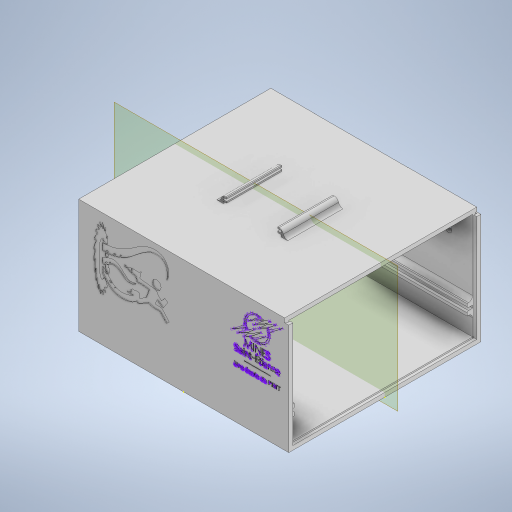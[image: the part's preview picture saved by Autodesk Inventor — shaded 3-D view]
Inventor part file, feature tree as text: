
AUTODESK INVENTOR PART (.ipt)
format: ipt  version: 2023 (Build 270158000, 158)  size: 8,297,472 bytes
history: native  units: mm
features: sketch x25, extrude x21, other x5, fillet x3, projected_geometry x3, sweep x1
ambient origin geometry x8: Origin, YZ Plane, XZ Plane, XY Plane, X Axis, Y Axis, Z Axis, Center Point
bodies: Solide1 (feature_tree)
feature tree (58):
  sketch  "Esquisse1"
  extrude  "Extrusion1"  Depth=133.2mm
  extrude  "Extrusion2"  Depth=146.2mm
  extrude  "Extrusion3"  Depth=3.0mm
  sketch  "Esquisse3"
  extrude  "Extrusion4"  Depth=3.0mm TaperAngle=0.0deg
  extrude  "Extrusion5"  Depth=80.0mm TaperAngle=0.0deg
  extrude  "Extrusion6"  Depth=3.0mm TaperAngle=0.0deg
  extrude  "Extrusion7"  Depth=3.0mm
  extrude  "Extrusion8"  Depth=3.0mm
  fillet  "Congé1"  Radius=3.0mm
  fillet  "Congé2"  Radius=3.0mm
  sketch  "Esquisse9"
  other  "Plan de construction1"
  sketch  "Esquisse11"
  other  "Plan de construction2"
  sweep  "Balayage2"
  sketch  "Esquisse14"
  extrude  "Extrusion9"  Depth=1.0mm
  sketch  "Esquisse15"
  sketch  "Esquisse16"
  extrude  "Extrusion11"  Depth=2.0mm TaperAngle=0.0deg
  extrude  "Extrusion12"  Depth=1.0mm
  sketch  "Esquisse17"
  extrude  "Extrusion13"  Depth=2.0mm TaperAngle=0.0deg
  extrude  "Extrusion14"  Depth=2.0mm TaperAngle=0.0deg
  fillet  "Congé3"  Radius=4.0mm
  extrude  "Extrusion15"  Depth=4.0mm
  extrude  "Extrusion16"  Depth=1.9mm
  extrude  "Extrusion18"  Depth=3.0mm
  sketch  "Esquisse24"
  extrude  "Extrusion19"  Depth=3.0mm
  extrude  "Extrusion20"  Depth=20.0mm
  extrude  "Extrusion21"  Depth=2.0mm TaperAngle=0.0deg
  sketch  "Esquisse26"
  sketch  "Esquisse27"
  extrude  "Extrusion22"  Depth=3.0mm
  extrude  "Extrusion23"  Depth=1.0mm
  sketch  "Esquisse29"
  other  "Gravure1"
  other  "Gravure2"
  other  "Gravure3"
  sketch  "Esquisse2"
  sketch  "Esquisse4"
  sketch  "Esquisse5"
  sketch  "Esquisse6"
  sketch  "Esquisse7"
  sketch  "Esquisse8"
  sketch  "Esquisse13"
  sketch  "Esquisse19"
  sketch  "Esquisse20"
  sketch  "Esquisse21"
  sketch  "Esquisse23"
  sketch  "Esquisse25"
  projected_geometry  "Boucle projetée2"
  projected_geometry  "Boucle projetée3"
  projected_geometry  "Boucle projetée4"
  sketch  "Esquisse30"
